# Revit family: Interceptor-Solids-Zurn-Z1180
name_source: partatom
category: Plumbing Fixtures
units: mm (PartAtom-declared; Revit-internal decimal feet)

## family parameters
Always vertical = Yes
Cut with Voids When Loaded = No
Maintain Annotation Orientation = No
OmniClass Number = 23.45.30.00
OmniClass Title = Washing and Waste Disposal Equipment
Part Type = Normal
Room Calculation Point = No
Round Connector Dimension = Use Radius
Shared = No
Work Plane-Based = No

## types (2) — shared parameters
Approx. Weight (Lbs) = 6
Assembly Code = D2090300
CW Connection = No
CWFU = 1
Default Elevation = 15 "
Description = Z1180 Solids interceptor
Flow = 15 GPM
HW Connection = No
HWFU = 1
Handle Material = ABS - Zurn - Acrylonitrile Butadiene Styrene - Black
Main Material = Polyester- Zurn - Glass-fibre reinforced- Grey
Manufacturer = Zurn
Manufacturer Brand = Zurn Water, LLC
Model = Z1180
Modified Date = 07/14/2025
Product Documentation Link = https://files.zurn.com
Product Installation Sheet URL = https://files.zurn.com
Product Page URL = https://www.zurn.com
Product data url = https://www.bimobject.com
URL = http://www.zurn.com
Vent Connection = No
Waste Connection = Yes
zero-valued in all types: WFU

## per-type parameters (varying)
| type | Connector Radius | Outlet Outer Diameter | Outlet Size |
| Z1180-2" Inlet/outlet | 1 " | 2.375 " | 2 " |
| Z1180-1-1/2" Inlet/outlet | 0.75 " | 1.9 " | 1.5 " |

## geometry (parser evidence)
native form markers: Blend x4, Sweep x3
no freeform markers — native parametric forms only
